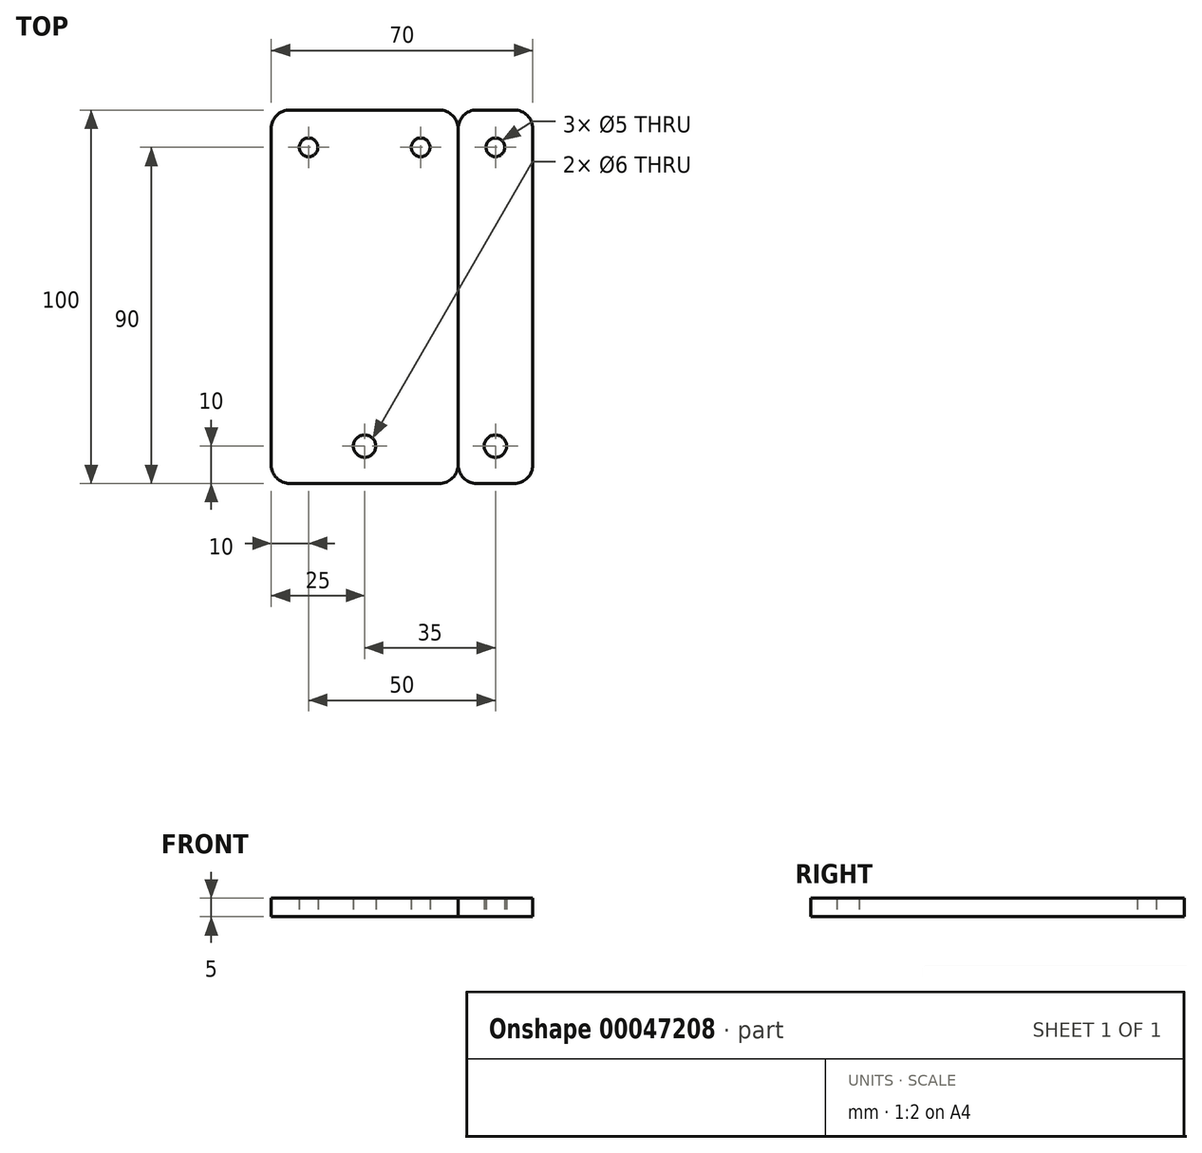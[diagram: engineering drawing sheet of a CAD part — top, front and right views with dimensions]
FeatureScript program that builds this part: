
annotation { "Feature Type Name" : "Feature", "Feature Type Description" : "" }
export const myFeature = defineFeature(function(context is Context, id is Id, definition is map)
    precondition{}
    {
        {
            var Q0;
            Q0=qCreatedBy(makeId("Top.planeOp"),FACE);
            var sketch = newSketch(context, id + "F0", { "sketchPlane" : qUnion([Q0])});
            skLineSegment(sketch, "E0.bottom", {"start": v(5, 0) * mm, "end": v(15, 0) * mm});
            skLineSegment(sketch, "E0.top", {"start": v(5, 100) * mm, "end": v(15, 100) * mm});
            skLineSegment(sketch, "E0.left", {"start": v(0, 5) * mm, "end": v(0, 95) * mm});
            skLineSegment(sketch, "E0.right", {"start": v(20, 5) * mm, "end": v(20, 95) * mm});
            skLineSegment(sketch, "E1", {"start": v(10, 114.7) * mm, "end": v(10, -35.12) * mm, "construction": true});
            skCircle(sketch, "E2", {"center": v(10, 10) * mm, "radius": 3 * mm});
            skCircle(sketch, "E3", {"center": v(10, 90) * mm, "radius": 2.5 * mm});
            skPoint(sketch, "E4.visualSharp", {"position": v(0, 100) * mm});
            skArc(sketch, "E4.filletArc", {"start": v(5, 100) * mm, "mid": v(1.46, 98.54) * mm, "end": v(0, 95) * mm});
            skPoint(sketch, "E5.visualSharp", {"position": v(20, 100) * mm});
            skArc(sketch, "E5.filletArc", {"start": v(20, 95) * mm, "mid": v(18.54, 98.54) * mm, "end": v(15, 100) * mm});
            skPoint(sketch, "E6.visualSharp", {"position": v(20, 0) * mm});
            skArc(sketch, "E6.filletArc", {"start": v(15, 0) * mm, "mid": v(18.54, 1.46) * mm, "end": v(20, 5) * mm});
            skPoint(sketch, "E7.visualSharp", {"position": v(0, 0) * mm});
            skArc(sketch, "E7.filletArc", {"start": v(0, 5) * mm, "mid": v(1.46, 1.46) * mm, "end": v(5, 0) * mm});
            skSolve(sketch);
        }
        {
            var Q0;
            Q0=makeQuery(id+"F0.imprint","IMPRINT",FACE,{"disambiguationData":[TD([[makeQuery(id+"F0.imprint","IMPRINT",EDGE,{"derivedFrom":sQuery(id+"F0.wireOp",EDGE,"E0.bottom")}),1.0]])]});
            extrude(context, id + "F1", {"entities" : qUnion([Q0]), "depth" : 5 * mm});
        }
        {
            var Q0;
            Q0=qCreatedBy(makeId("Top.planeOp"),FACE);
            var sketch = newSketch(context, id + "F2", { "sketchPlane" : qUnion([Q0])});
            skLineSegment(sketch, "E8.bottom", {"start": v(-5, 0) * mm, "end": v(-45, 0) * mm});
            skLineSegment(sketch, "E8.top", {"start": v(-5, 100) * mm, "end": v(-45, 100) * mm});
            skLineSegment(sketch, "E8.left", {"start": v(0, 5) * mm, "end": v(0, 95) * mm});
            skLineSegment(sketch, "E8.right", {"start": v(-50, 5) * mm, "end": v(-50, 95) * mm});
            skCircle(sketch, "E9", {"center": v(-10, 90) * mm, "radius": 2.5 * mm});
            skCircle(sketch, "E10", {"center": v(-25, 10) * mm, "radius": 3 * mm});
            skCircle(sketch, "E11", {"center": v(-40, 90) * mm, "radius": 2.5 * mm});
            skPoint(sketch, "E12.visualSharp", {"position": v(-50, 100) * mm});
            skArc(sketch, "E12.filletArc", {"start": v(-45, 100) * mm, "mid": v(-48.54, 98.54) * mm, "end": v(-50, 95) * mm});
            skPoint(sketch, "E13.visualSharp", {"position": v(0, 100) * mm});
            skArc(sketch, "E13.filletArc", {"start": v(0, 95) * mm, "mid": v(-1.46, 98.54) * mm, "end": v(-5, 100) * mm});
            skPoint(sketch, "E14.visualSharp", {"position": v(0, 0) * mm});
            skArc(sketch, "E14.filletArc", {"start": v(-5, 0) * mm, "mid": v(-1.46, 1.46) * mm, "end": v(0, 5) * mm});
            skPoint(sketch, "E15.visualSharp", {"position": v(-50, 0) * mm});
            skArc(sketch, "E15.filletArc", {"start": v(-50, 5) * mm, "mid": v(-48.54, 1.46) * mm, "end": v(-45, 0) * mm});
            skSolve(sketch);
        }
        {
            var Q0;
            Q0=makeQuery(id+"F2.imprint","IMPRINT",FACE,{"disambiguationData":[TD([[makeQuery(id+"F2.imprint","IMPRINT",EDGE,{"derivedFrom":sQuery(id+"F2.wireOp",EDGE,"E8.bottom")}),-1.0]])]});
            extrude(context, id + "F3", {"entities" : qUnion([Q0]), "depth" : 5 * mm});
        }
    });
